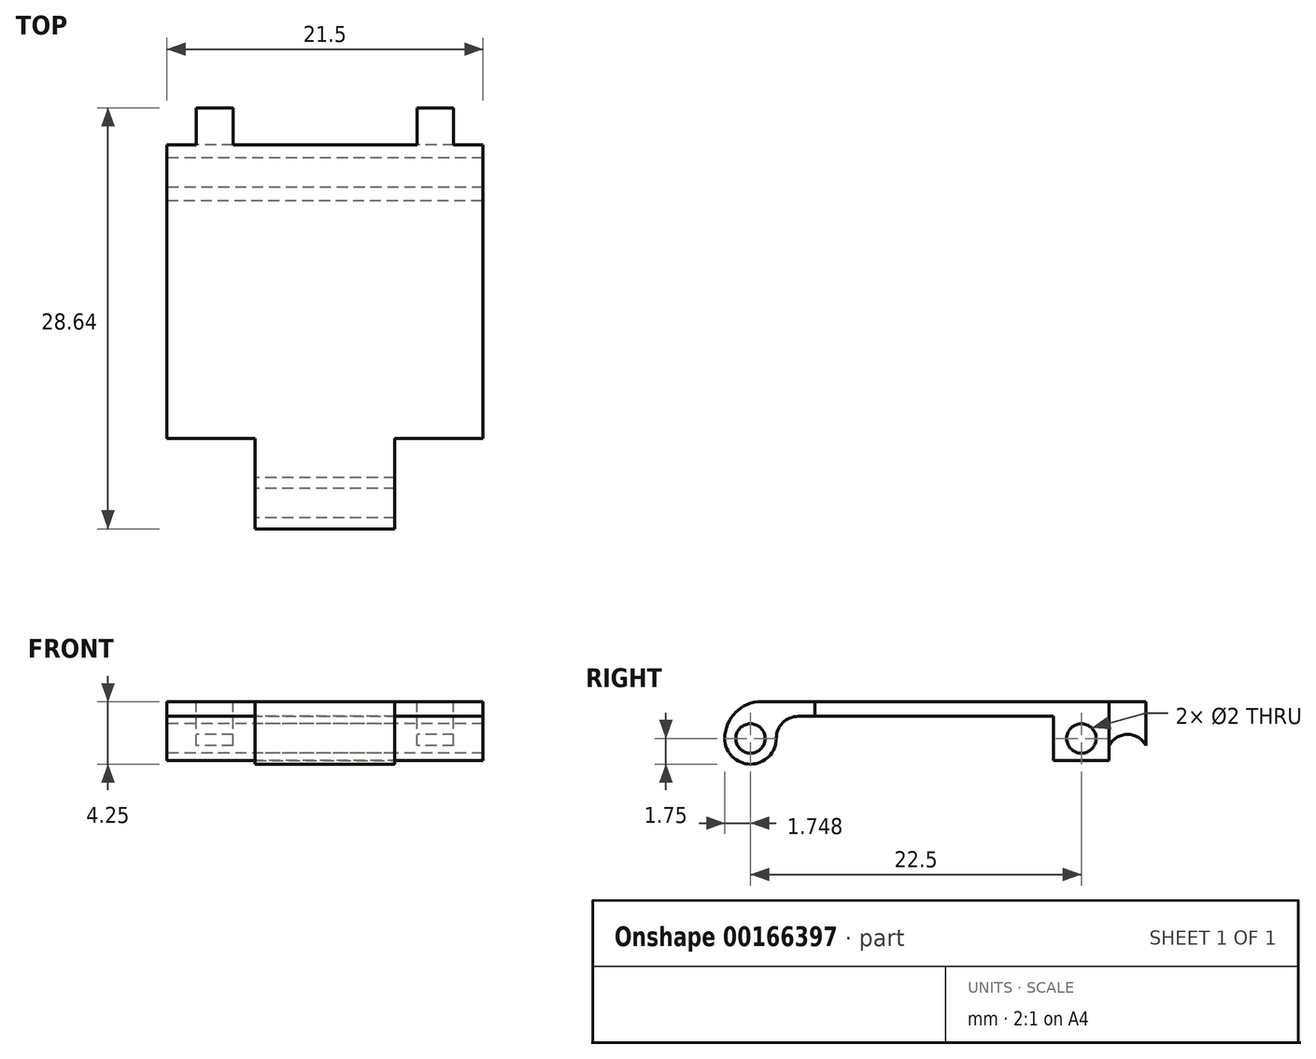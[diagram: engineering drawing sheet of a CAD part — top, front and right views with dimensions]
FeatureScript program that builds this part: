
annotation { "Feature Type Name" : "Feature", "Feature Type Description" : "" }
export const myFeature = defineFeature(function(context is Context, id is Id, definition is map)
    precondition{}
    {
        {
            var Q0;
            Q0=qCreatedBy(makeId("Top.planeOp"),FACE);
            var sketch = newSketch(context, id + "F0", { "sketchPlane" : qUnion([Q0])});
            skLineSegment(sketch, "E0.bottom", {"start": v(10.75, -10) * mm, "end": v(-10.75, -10) * mm});
            skLineSegment(sketch, "E0.top", {"start": v(10.75, 10) * mm, "end": v(-10.75, 10) * mm});
            skLineSegment(sketch, "E0.left", {"start": v(10.75, -10) * mm, "end": v(10.75, 10) * mm});
            skLineSegment(sketch, "E0.right", {"start": v(-10.75, -10) * mm, "end": v(-10.75, 10) * mm});
            skPoint(sketch, "E0.middle", {"position": v(0, 0) * mm});
            skSolve(sketch);
        }
        {
            var Q0;
            Q0=makeQuery(id+"F0.imprint","IMPRINT",FACE,{"disambiguationData":[TD([[makeQuery(id+"F0.imprint","IMPRINT",EDGE,{"derivedFrom":sQuery(id+"F0.wireOp",EDGE,"E0.bottom")}),-1.0]])]});
            var sketch = newSketch(context, id + "F1", { "sketchPlane" : qUnion([Q0])});
            skLineSegment(sketch, "E1.0", {"start": v(10.75, 10) * mm, "end": v(-10.75, 10) * mm});
            skLineSegment(sketch, "E1.1", {"start": v(-10.75, -10) * mm, "end": v(-10.75, 10) * mm});
            skLineSegment(sketch, "E1.2", {"start": v(10.75, -10) * mm, "end": v(10.75, 10) * mm});
            skLineSegment(sketch, "E2.bottom", {"start": v(-10.75, 10) * mm, "end": v(10.75, 10) * mm});
            skLineSegment(sketch, "E2.top", {"start": v(-10.75, 6.22) * mm, "end": v(10.75, 6.22) * mm});
            skLineSegment(sketch, "E2.left", {"start": v(-10.75, 10) * mm, "end": v(-10.75, 6.22) * mm});
            skLineSegment(sketch, "E2.right", {"start": v(10.75, 10) * mm, "end": v(10.75, 6.22) * mm});
            skSolve(sketch);
        }
        {
            var Q0;
            Q0 = qSketchRegion(id + "F1", true);
            extrude(context, id + "F2", {"entities" : qUnion([Q0]), "oppositeDirection" : true, "depth" : 3 * mm});
        }
        {
            var Q0;
            Q0=makeQuery(id+"F0.imprint","IMPRINT",FACE,{"disambiguationData":[TD([[makeQuery(id+"F0.imprint","IMPRINT",EDGE,{"derivedFrom":sQuery(id+"F0.wireOp",EDGE,"E0.bottom")}),-1.0]])]});
            extrude(context, id + "F3", {"entities" : qUnion([Q0]), "operationType" : NewBodyOperationType.ADD, "depth" : 1 * mm});
        }
        {
            var Q0;
            Q0=makeQuery(id+"F3.boolean.opBoolean","MERGE",FACE,{"derivedFrom":[makeQuery(id+"F2.opExtrude","SWEPT_FACE",FACE,{"disambiguationData":[OSD([sQuery(id+"F1.wireOp",EDGE,"E2.left")])]}),makeQuery(id+"F3.opExtrude","SWEPT_FACE",FACE,{"disambiguationData":[OSD([sQuery(id+"F0.wireOp",EDGE,"E0.right")])]})]});
            var sketch = newSketch(context, id + "F4", { "sketchPlane" : qUnion([Q0])});
            skCircle(sketch, "E3", {"center": v(-8.1, -1.5) * mm, "radius": 1 * mm});
            skLineSegment(sketch, "E4", {"start": v(-6.22, 0) * mm, "end": v(-6.22, -1.5) * mm});
            skLineSegment(sketch, "E5", {"start": v(-7.72, -3) * mm, "end": v(-8.5, -3) * mm});
            skLineSegment(sketch, "E6", {"start": v(-10, -1.5) * mm, "end": v(-10, 0) * mm});
            skPoint(sketch, "E7.visualSharp", {"position": v(-10, -3) * mm});
            skArc(sketch, "E7.filletArc", {"start": v(-10, -1.5) * mm, "mid": v(-9.56, -2.56) * mm, "end": v(-8.5, -3) * mm});
            skPoint(sketch, "E8.visualSharp", {"position": v(-6.22, -3) * mm});
            skArc(sketch, "E8.filletArc", {"start": v(-7.72, -3) * mm, "mid": v(-6.66, -2.56) * mm, "end": v(-6.22, -1.5) * mm});
            skSolve(sketch);
        }
        {
            var Q0;
            Q0 = qSketchRegion(id + "F4", true);
            extrude(context, id + "F5", {"entities" : qUnion([Q0]), "operationType" : NewBodyOperationType.REMOVE, "oppositeDirection" : true, "depth" : 21.5 * mm});
        }
        {
            var Q0;
            Q0=qCreatedBy(makeId("Right.planeOp"),FACE);
            var sketch = newSketch(context, id + "F6", { "sketchPlane" : qUnion([Q0])});
            skCircle(sketch, "E9.0", {"center": v(8.1, -1.5) * mm, "radius": 1 * mm});
            skCircle(sketch, "E10", {"center": v(-14.4, -1.5) * mm, "radius": 1 * mm});
            skArc(sketch, "E11", {"start": v(-16.14, -1.5) * mm, "mid": v(-14.4, -3.25) * mm, "end": v(-12.64, -1.5) * mm});
            skLineSegment(sketch, "E12.0", {"start": v(-10, 1) * mm, "end": v(10, 1) * mm});
            skLineSegment(sketch, "E12.1", {"start": v(-10, 1) * mm, "end": v(-10, 0) * mm});
            skLineSegment(sketch, "E12.2.0", {"start": v(6.22, -3) * mm, "end": v(6.22, 0) * mm});
            skLineSegment(sketch, "E12.2.1", {"start": v(6.22, 0) * mm, "end": v(-10, 0) * mm});
            skLineSegment(sketch, "E12.2.2", {"start": v(-10, 0) * mm, "end": v(-10, 1) * mm});
            skLineSegment(sketch, "E12.2.3", {"start": v(-10, 1) * mm, "end": v(10, 1) * mm});
            skLineSegment(sketch, "E12.2.4", {"start": v(10, 1) * mm, "end": v(10, -3) * mm});
            skLineSegment(sketch, "E12.2.5", {"start": v(10, -3) * mm, "end": v(6.22, -3) * mm});
            skPoint(sketch, "E12.3", {"position": v(-10, 0.5) * mm});
            skLineSegment(sketch, "E13", {"start": v(-16.14, -1.5) * mm, "end": v(-16.14, -1.5) * mm});
            skLineSegment(sketch, "E14", {"start": v(-10, 1) * mm, "end": v(-13.64, 1) * mm});
            skLineSegment(sketch, "E15", {"start": v(-10, 0) * mm, "end": v(-11.14, 0) * mm});
            skArc(sketch, "E16.filletArc", {"start": v(-13.64, 1) * mm, "mid": v(-15.4, 0.27) * mm, "end": v(-16.14, -1.5) * mm});
            skPoint(sketch, "E17.visualSharp", {"position": v(-13.5, 0) * mm});
            skArc(sketch, "E17.filletArc", {"start": v(-11.14, 0) * mm, "mid": v(-12.2, -0.44) * mm, "end": v(-12.64, -1.5) * mm});
            skSolve(sketch);
        }
        {
            var Q0;
            Q0 = qSketchRegion(id + "F6", true);
            extrude(context, id + "F7", {"entities" : qUnion([Q0]), "operationType" : NewBodyOperationType.ADD, "endBound" : BoundingType.SYMMETRIC, "depth" : 9.5 * mm});
        }
        {
            var Q0;
            Q0=makeQuery(id+"F7.boolean.opBoolean","MERGE",FACE,{"derivedFrom":[makeQuery(id+"F3.opExtrude","CAP_FACE",FACE,{"disambiguationData":[OSD([sQuery(id+"F0.wireOp",EDGE,"E0.bottom"),sQuery(id+"F0.wireOp",EDGE,"E0.top"),sQuery(id+"F0.wireOp",EDGE,"E0.left"),sQuery(id+"F0.wireOp",EDGE,"E0.right")])],"isStart":false}),makeQuery(id+"F7.opExtrude","SWEPT_FACE",FACE,{"disambiguationData":[OSD([sQuery(id+"F6.wireOp",EDGE,"E12.2.3"),sQuery(id+"F6.wireOp",EDGE,"E14")])]})]});
            var sketch = newSketch(context, id + "F8", { "sketchPlane" : qUnion([Q0])});
            skLineSegment(sketch, "E18.bottom", {"start": v(-8.75, 10) * mm, "end": v(-6.25, 10) * mm});
            skLineSegment(sketch, "E18.top", {"start": v(-8.75, 12.5) * mm, "end": v(-6.25, 12.5) * mm});
            skLineSegment(sketch, "E18.left", {"start": v(-8.75, 10) * mm, "end": v(-8.75, 12.5) * mm});
            skLineSegment(sketch, "E18.right", {"start": v(-6.25, 10) * mm, "end": v(-6.25, 12.5) * mm});
            skLineSegment(sketch, "E19.bottom", {"start": v(8.75, 10) * mm, "end": v(6.25, 10) * mm});
            skLineSegment(sketch, "E19.top", {"start": v(8.75, 12.5) * mm, "end": v(6.25, 12.5) * mm});
            skLineSegment(sketch, "E19.left", {"start": v(8.75, 10) * mm, "end": v(8.75, 12.5) * mm});
            skLineSegment(sketch, "E19.right", {"start": v(6.25, 10) * mm, "end": v(6.25, 12.5) * mm});
            skSolve(sketch);
        }
        {
            var Q0;
            Q0=makeQuery(id+"F8.imprint","IMPRINT",FACE,{"disambiguationData":[TD([[makeQuery(id+"F8.imprint","IMPRINT",EDGE,{"derivedFrom":sQuery(id+"F8.wireOp",EDGE,"E18.bottom")}),-1.0]])]});
            var Q1;
            Q1=makeQuery(id+"F8.imprint","IMPRINT",FACE,{"disambiguationData":[TD([[makeQuery(id+"F8.imprint","IMPRINT",EDGE,{"derivedFrom":sQuery(id+"F8.wireOp",EDGE,"E19.bottom")}),-1.0]])]});
            extrude(context, id + "F9", {"entities" : qUnion([Q0, Q1]), "operationType" : NewBodyOperationType.ADD, "oppositeDirection" : true, "depth" : 3 * mm});
        }
        {
            var Q0;
            Q0=makeQuery(id+"F9.opExtrude","SWEPT_FACE",FACE,{"disambiguationData":[OSD([sQuery(id+"F8.wireOp",EDGE,"E18.left")])]});
            var sketch = newSketch(context, id + "F10", { "sketchPlane" : qUnion([Q0])});
            skArc(sketch, "E20", {"start": v(-10, -2) * mm, "mid": v(-11.25, -1.22) * mm, "end": v(-12.5, -2) * mm});
            skSolve(sketch);
        }
        {
            var Q0;
            Q0 = qSketchRegion(id + "F10", true);
            var Q1;
            Q1=makeQuery(id+"F10.imprint","IMPRINT",FACE,{"disambiguationData":[TD([[makeQuery(id+"F10.imprint","IMPRINT",EDGE,{"derivedFrom":sQuery(id+"F10.wireOp",EDGE,"E20")}),1.0]])]});
            extrude(context, id + "F11", {"entities" : qUnion([Q0, Q1]), "operationType" : NewBodyOperationType.REMOVE, "oppositeDirection" : true, "depth" : 25 * mm});
        }
    });
